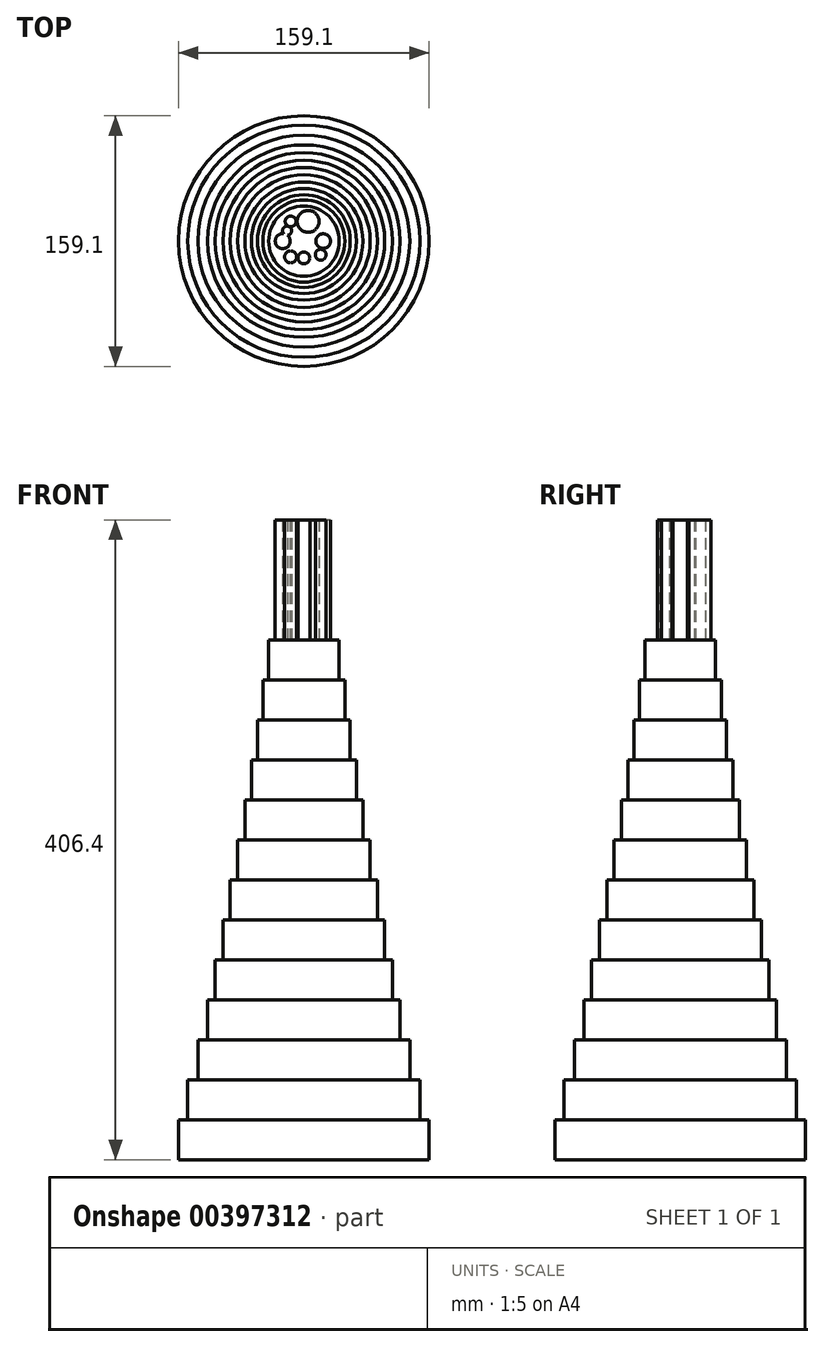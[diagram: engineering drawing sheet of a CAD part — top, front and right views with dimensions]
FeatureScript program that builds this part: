
annotation { "Feature Type Name" : "Feature", "Feature Type Description" : "" }
export const myFeature = defineFeature(function(context is Context, id is Id, definition is map)
    precondition{}
    {
        {
            var Q0;
            Q0=qCreatedBy(makeId("Top.planeOp"),FACE);
            var sketch = newSketch(context, id + "F0", { "sketchPlane" : qUnion([Q0])});
            skCircle(sketch, "E0", {"center": v(0, 0) * mm, "radius": 79.55 * mm});
            skSolve(sketch);
        }
        {
            var Q0;
            Q0 = qSketchRegion(id + "F0", true);
            extrude(context, id + "F1", {"entities" : qUnion([Q0]), "depth" : 25.4 * mm});
        }
        {
            var Q0;
            Q0=makeQuery(id+"F1.opExtrude","CAP_FACE",FACE,{"disambiguationData":[OSD([sQuery(id+"F0.wireOp",EDGE,"E0")])],"isStart":false});
            var sketch = newSketch(context, id + "F2", { "sketchPlane" : qUnion([Q0])});
            skCircle(sketch, "E1", {"center": v(0, 0) * mm, "radius": 73.75 * mm});
            skSolve(sketch);
        }
        {
            var Q0;
            Q0 = qSketchRegion(id + "F2", true);
            extrude(context, id + "F3", {"entities" : qUnion([Q0]), "operationType" : NewBodyOperationType.ADD, "depth" : 25.4 * mm});
        }
        {
            var Q0;
            Q0=makeQuery(id+"F3.opExtrude","CAP_FACE",FACE,{"disambiguationData":[OSD([sQuery(id+"F2.wireOp",EDGE,"E1")])],"isStart":false});
            var sketch = newSketch(context, id + "F4", { "sketchPlane" : qUnion([Q0])});
            skCircle(sketch, "E2", {"center": v(0, 0) * mm, "radius": 67.27 * mm});
            skSolve(sketch);
        }
        {
            var Q0;
            Q0 = qSketchRegion(id + "F4", true);
            extrude(context, id + "F5", {"entities" : qUnion([Q0]), "operationType" : NewBodyOperationType.ADD, "depth" : 25.4 * mm});
        }
        {
            var Q0;
            Q0=makeQuery(id+"F5.opExtrude","CAP_FACE",FACE,{"disambiguationData":[OSD([sQuery(id+"F4.wireOp",EDGE,"E2")])],"isStart":false});
            var sketch = newSketch(context, id + "F6", { "sketchPlane" : qUnion([Q0])});
            skCircle(sketch, "E3", {"center": v(0, 0) * mm, "radius": 61.1 * mm});
            skSolve(sketch);
        }
        {
            var Q0;
            Q0 = qSketchRegion(id + "F6", true);
            extrude(context, id + "F7", {"entities" : qUnion([Q0]), "operationType" : NewBodyOperationType.ADD, "depth" : 25.4 * mm});
        }
        {
            var Q0;
            Q0=makeQuery(id+"F7.opExtrude","CAP_FACE",FACE,{"disambiguationData":[OSD([sQuery(id+"F6.wireOp",EDGE,"E3")])],"isStart":false});
            var sketch = newSketch(context, id + "F8", { "sketchPlane" : qUnion([Q0])});
            skCircle(sketch, "E4", {"center": v(0, 0) * mm, "radius": 56.3 * mm});
            skSolve(sketch);
        }
        {
            var Q0;
            Q0 = qSketchRegion(id + "F8", true);
            extrude(context, id + "F9", {"entities" : qUnion([Q0]), "operationType" : NewBodyOperationType.ADD, "depth" : 25.4 * mm});
        }
        {
            var Q0;
            Q0=makeQuery(id+"F9.opExtrude","CAP_FACE",FACE,{"disambiguationData":[OSD([sQuery(id+"F8.wireOp",EDGE,"E4")])],"isStart":false});
            var sketch = newSketch(context, id + "F10", { "sketchPlane" : qUnion([Q0])});
            skCircle(sketch, "E5", {"center": v(0, 0) * mm, "radius": 51.34 * mm});
            skSolve(sketch);
        }
        {
            var Q0;
            Q0 = qSketchRegion(id + "F10", true);
            extrude(context, id + "F11", {"entities" : qUnion([Q0]), "operationType" : NewBodyOperationType.ADD, "depth" : 25.4 * mm});
        }
        {
            var Q0;
            Q0=makeQuery(id+"F11.opExtrude","CAP_FACE",FACE,{"disambiguationData":[OSD([sQuery(id+"F10.wireOp",EDGE,"E5")])],"isStart":false});
            var sketch = newSketch(context, id + "F12", { "sketchPlane" : qUnion([Q0])});
            skCircle(sketch, "E6", {"center": v(0, 0) * mm, "radius": 46.76 * mm});
            skSolve(sketch);
        }
        {
            var Q0;
            Q0 = qSketchRegion(id + "F12", true);
            extrude(context, id + "F13", {"entities" : qUnion([Q0]), "operationType" : NewBodyOperationType.ADD, "depth" : 25.4 * mm});
        }
        {
            var Q0;
            Q0=makeQuery(id+"F13.opExtrude","CAP_FACE",FACE,{"disambiguationData":[OSD([sQuery(id+"F12.wireOp",EDGE,"E6")])],"isStart":false});
            var sketch = newSketch(context, id + "F14", { "sketchPlane" : qUnion([Q0])});
            skCircle(sketch, "E7", {"center": v(0, 0) * mm, "radius": 42.1 * mm});
            skSolve(sketch);
        }
        {
            var Q0;
            Q0 = qSketchRegion(id + "F14", true);
            extrude(context, id + "F15", {"entities" : qUnion([Q0]), "operationType" : NewBodyOperationType.ADD, "depth" : 25.4 * mm});
        }
        {
            var Q0;
            Q0=makeQuery(id+"F15.opExtrude","CAP_FACE",FACE,{"disambiguationData":[OSD([sQuery(id+"F14.wireOp",EDGE,"E7")])],"isStart":false});
            var sketch = newSketch(context, id + "F16", { "sketchPlane" : qUnion([Q0])});
            skCircle(sketch, "E8", {"center": v(0, 0) * mm, "radius": 37.5 * mm});
            skSolve(sketch);
        }
        {
            var Q0;
            Q0 = qSketchRegion(id + "F16", true);
            extrude(context, id + "F17", {"entities" : qUnion([Q0]), "operationType" : NewBodyOperationType.ADD, "depth" : 25.4 * mm});
        }
        {
            var Q0;
            Q0=makeQuery(id+"F17.opExtrude","CAP_FACE",FACE,{"disambiguationData":[OSD([sQuery(id+"F16.wireOp",EDGE,"E8")])],"isStart":false});
            var sketch = newSketch(context, id + "F18", { "sketchPlane" : qUnion([Q0])});
            skCircle(sketch, "E9", {"center": v(0, 0) * mm, "radius": 33.34 * mm});
            skSolve(sketch);
        }
        {
            var Q0;
            Q0 = qSketchRegion(id + "F18", true);
            extrude(context, id + "F19", {"entities" : qUnion([Q0]), "operationType" : NewBodyOperationType.ADD, "depth" : 25.4 * mm});
        }
        {
            var Q0;
            Q0=makeQuery(id+"F19.opExtrude","CAP_FACE",FACE,{"disambiguationData":[OSD([sQuery(id+"F18.wireOp",EDGE,"E9")])],"isStart":false});
            var sketch = newSketch(context, id + "F20", { "sketchPlane" : qUnion([Q0])});
            skCircle(sketch, "E10", {"center": v(0, 0) * mm, "radius": 29.43 * mm});
            skSolve(sketch);
        }
        {
            var Q0;
            Q0 = qSketchRegion(id + "F20", true);
            extrude(context, id + "F21", {"entities" : qUnion([Q0]), "operationType" : NewBodyOperationType.ADD, "depth" : 25.4 * mm});
        }
        {
            var Q0;
            Q0=makeQuery(id+"F21.opExtrude","CAP_FACE",FACE,{"disambiguationData":[OSD([sQuery(id+"F20.wireOp",EDGE,"E10")])],"isStart":false});
            var sketch = newSketch(context, id + "F22", { "sketchPlane" : qUnion([Q0])});
            skCircle(sketch, "E11", {"center": v(0, 0) * mm, "radius": 26.09 * mm});
            skSolve(sketch);
        }
        {
            var Q0;
            Q0 = qSketchRegion(id + "F22", true);
            extrude(context, id + "F23", {"entities" : qUnion([Q0]), "operationType" : NewBodyOperationType.ADD, "depth" : 25.4 * mm});
        }
        {
            var Q0;
            Q0=makeQuery(id+"F23.opExtrude","CAP_FACE",FACE,{"disambiguationData":[OSD([sQuery(id+"F22.wireOp",EDGE,"E11")])],"isStart":false});
            var sketch = newSketch(context, id + "F24", { "sketchPlane" : qUnion([Q0])});
            skCircle(sketch, "E12", {"center": v(0, 0) * mm, "radius": 22.37 * mm});
            skSolve(sketch);
        }
        {
            var Q0;
            Q0 = qSketchRegion(id + "F24", true);
            extrude(context, id + "F25", {"entities" : qUnion([Q0]), "operationType" : NewBodyOperationType.ADD, "depth" : 25.4 * mm});
        }
        {
            var Q0;
            Q0=makeQuery(id+"F25.opExtrude","CAP_FACE",FACE,{"disambiguationData":[OSD([sQuery(id+"F24.wireOp",EDGE,"E12")])],"isStart":false});
            var sketch = newSketch(context, id + "F26", { "sketchPlane" : qUnion([Q0])});
            skCircle(sketch, "E13", {"center": v(-8.42, 12.52) * mm, "radius": 3.42 * mm});
            skCircle(sketch, "E14", {"center": v(-13.43, 0) * mm, "radius": 4.75 * mm});
            skCircle(sketch, "E15", {"center": v(-8.42, -10.01) * mm, "radius": 3.81 * mm});
            skCircle(sketch, "E16", {"center": v(12.29, 0) * mm, "radius": 4.64 * mm});
            skCircle(sketch, "E17", {"center": v(10.7, -8.65) * mm, "radius": 3.44 * mm});
            skCircle(sketch, "E18", {"center": v(0, -10.7) * mm, "radius": 3.75 * mm});
            skCircle(sketch, "E19", {"center": v(-10.7, 6.6) * mm, "radius": 2.88 * mm});
            skCircle(sketch, "E20", {"center": v(2.73, 12.52) * mm, "radius": 6.97 * mm});
            skSolve(sketch);
        }
        {
            var Q0;
            Q0 = qSketchRegion(id + "F26", true);
            extrude(context, id + "F27", {"entities" : qUnion([Q0]), "operationType" : NewBodyOperationType.ADD, "depth" : 76.2 * mm});
        }
    });
